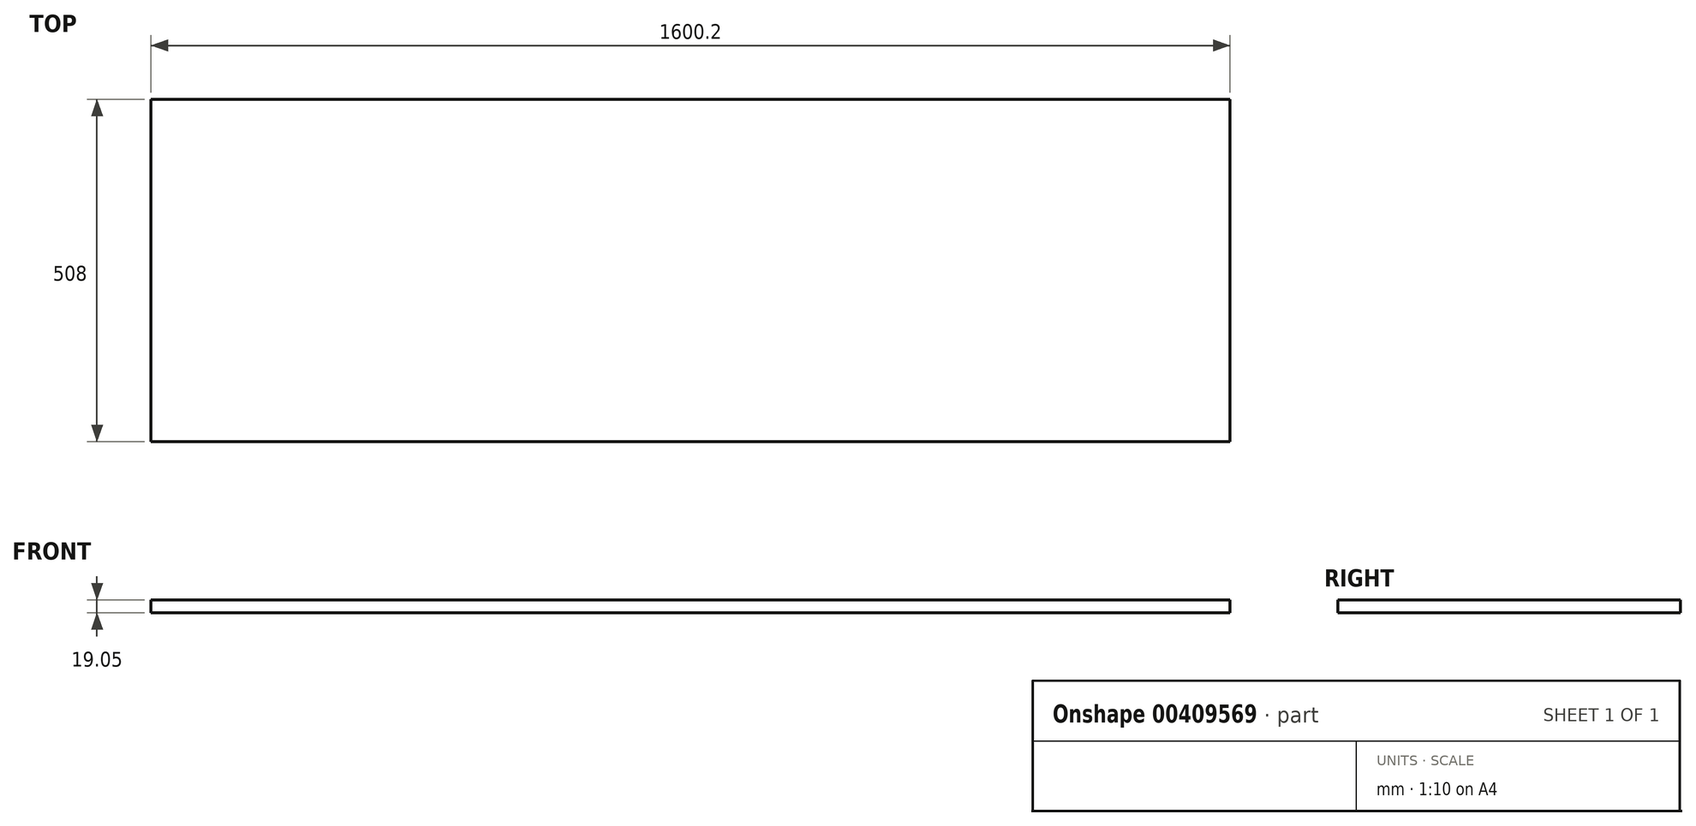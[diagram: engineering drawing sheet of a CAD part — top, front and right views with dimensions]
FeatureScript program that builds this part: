
annotation { "Feature Type Name" : "Feature", "Feature Type Description" : "" }
export const myFeature = defineFeature(function(context is Context, id is Id, definition is map)
    precondition{}
    {
        {
            var Q0;
            Q0=qCreatedBy(makeId("Top.planeOp"),FACE);
            var sketch = newSketch(context, id + "F0", { "sketchPlane" : qUnion([Q0])});
            skLineSegment(sketch, "E0.bottom", {"start": v(-837.9, -62.14) * mm, "end": v(762.3, -62.14) * mm});
            skLineSegment(sketch, "E0.top", {"start": v(-837.9, -570.14) * mm, "end": v(762.3, -570.14) * mm});
            skLineSegment(sketch, "E0.left", {"start": v(-837.9, -62.14) * mm, "end": v(-837.9, -570.14) * mm});
            skLineSegment(sketch, "E0.right", {"start": v(762.3, -62.14) * mm, "end": v(762.3, -570.14) * mm});
            skSolve(sketch);
        }
        {
            var Q0;
            Q0=makeQuery(id+"F0.imprint","IMPRINT",FACE,{"disambiguationData":[TD([[makeQuery(id+"F0.imprint","IMPRINT",EDGE,{"derivedFrom":sQuery(id+"F0.wireOp",EDGE,"E0.bottom")}),-1.0]])]});
            extrude(context, id + "F1", {"entities" : qUnion([Q0]), "depth" : 19.05 * mm});
        }
    });
